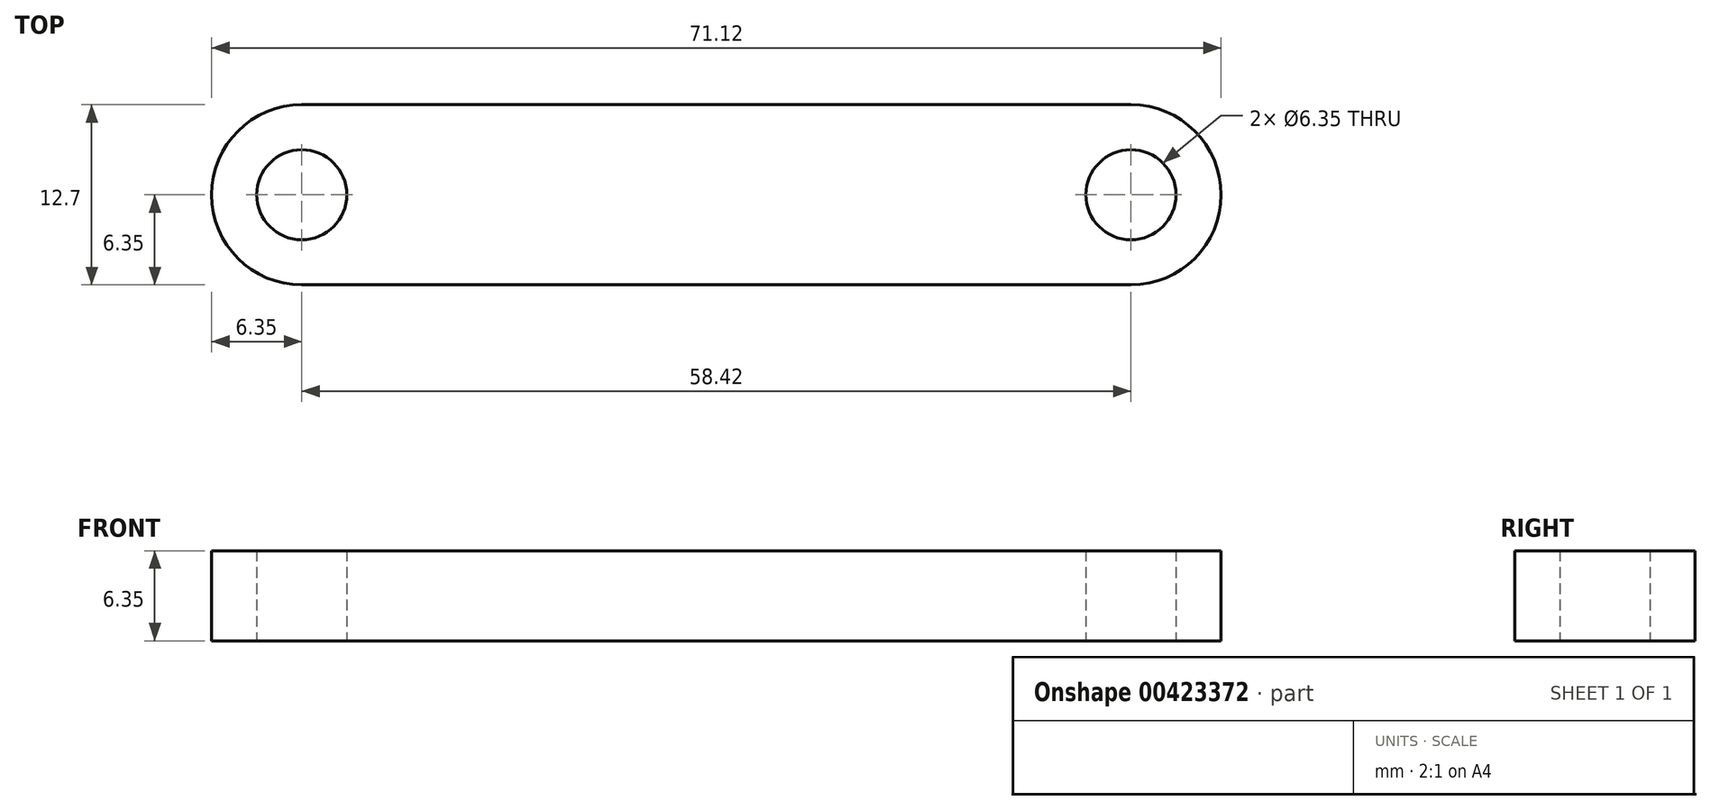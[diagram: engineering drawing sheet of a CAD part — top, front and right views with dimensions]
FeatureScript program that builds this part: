
annotation { "Feature Type Name" : "Feature", "Feature Type Description" : "" }
export const myFeature = defineFeature(function(context is Context, id is Id, definition is map)
    precondition{}
    {
        {
            var Q0;
            Q0=qCreatedBy(makeId("Top.planeOp"),FACE);
            var sketch = newSketch(context, id + "F0", { "sketchPlane" : qUnion([Q0])});
            skCircle(sketch, "E0", {"center": v(-29.21, 0) * mm, "radius": 3.18 * mm});
            skCircle(sketch, "E1", {"center": v(29.21, 0) * mm, "radius": 3.18 * mm});
            skCircle(sketch, "E2", {"center": v(-29.21, 0) * mm, "radius": 6.35 * mm});
            skCircle(sketch, "E3", {"center": v(29.21, 0) * mm, "radius": 6.35 * mm});
            skLineSegment(sketch, "E4", {"start": v(-29.21, 6.35) * mm, "end": v(29.21, 6.35) * mm});
            skLineSegment(sketch, "E5", {"start": v(29.21, -6.35) * mm, "end": v(-29.21, -6.35) * mm});
            skSolve(sketch);
        }
        {
            var Q0;
            Q0 = qSketchRegion(id + "F0", true);
            extrude(context, id + "F1", {"entities" : qUnion([Q0]), "depth" : 6.35 * mm});
        }
    });
